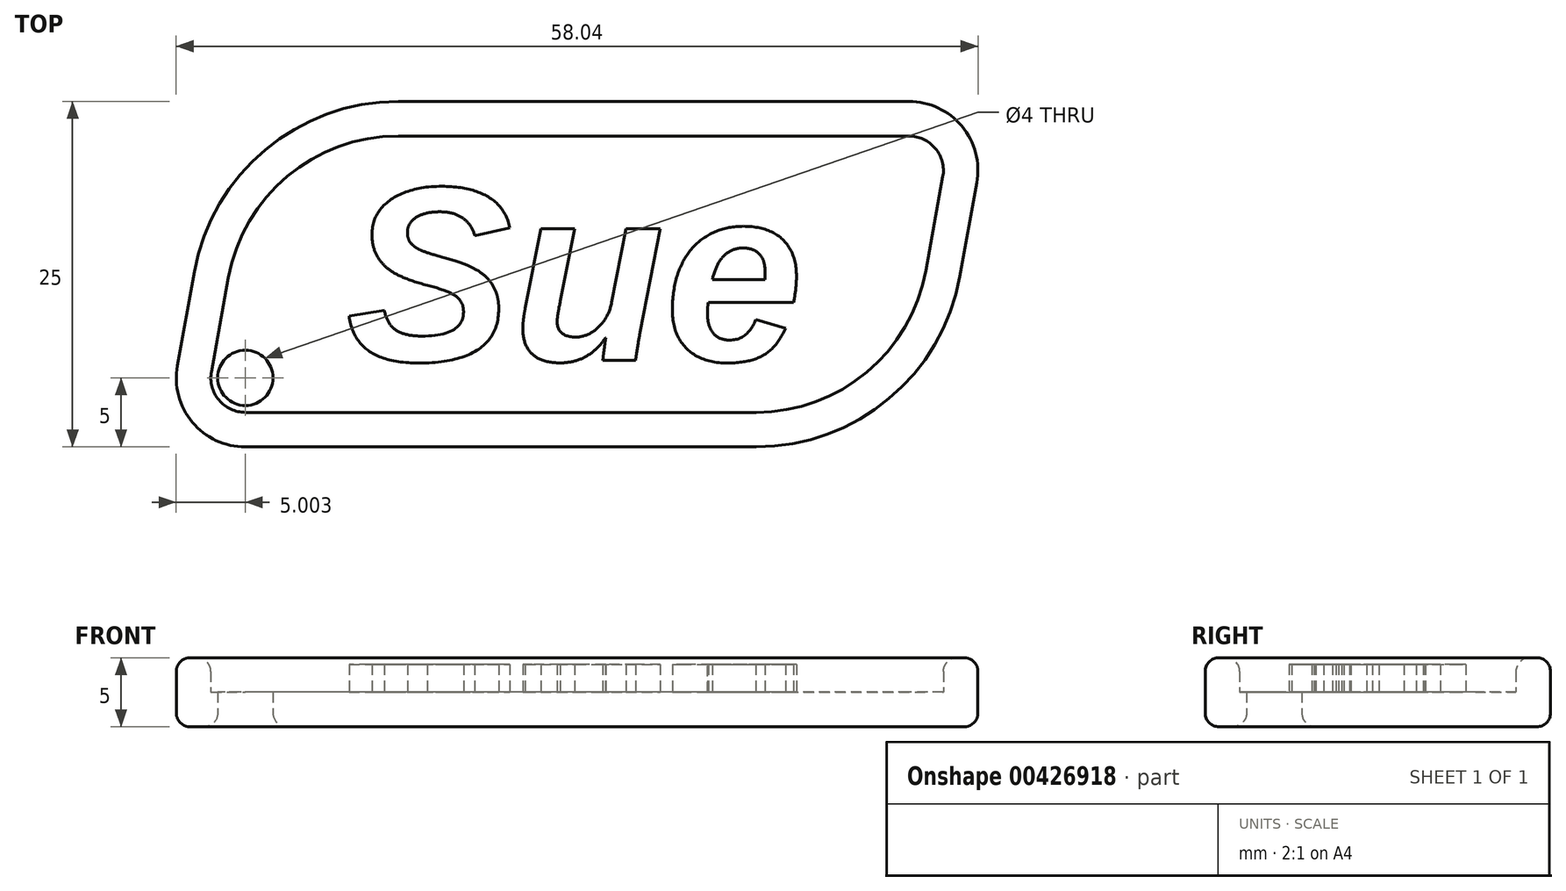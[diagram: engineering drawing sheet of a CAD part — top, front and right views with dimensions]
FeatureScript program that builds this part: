
annotation { "Feature Type Name" : "Feature", "Feature Type Description" : "" }
export const myFeature = defineFeature(function(context is Context, id is Id, definition is map)
    precondition{}
    {
        {
            var Q0;
            Q0=qCreatedBy(makeId("Top.planeOp"),FACE);
            var sketch = newSketch(context, id + "F0", { "sketchPlane" : qUnion([Q0])});
            skLineSegment(sketch, "E0.bottom", {"start": v(24.02, 12.5) * mm, "end": v(-12.95, 12.5) * mm});
            skLineSegment(sketch, "E0.top", {"start": v(12.95, -12.5) * mm, "end": v(-24.02, -12.5) * mm});
            skPoint(sketch, "E0.middle", {"position": v(0, 0) * mm});
            skLineSegment(sketch, "E1", {"start": v(-28.94, -6.61) * mm, "end": v(-27.71, 0.16) * mm});
            skLineSegment(sketch, "E2", {"start": v(28.94, 6.61) * mm, "end": v(27.71, -0.16) * mm});
            skPoint(sketch, "E3.orphan", {"position": v(-30.49, 12.5) * mm});
            skPoint(sketch, "E0.left.end.orphan", {"position": v(30.49, -12.5) * mm});
            skPoint(sketch, "E4.visualSharp", {"position": v(-25.49, 12.5) * mm});
            skArc(sketch, "E4.filletArc", {"start": v(-12.95, 12.5) * mm, "mid": v(-22.57, 9) * mm, "end": v(-27.71, 0.16) * mm});
            skPoint(sketch, "E5.visualSharp", {"position": v(25.49, -12.5) * mm});
            skArc(sketch, "E5.filletArc", {"start": v(12.95, -12.5) * mm, "mid": v(22.57, -9) * mm, "end": v(27.71, -0.16) * mm});
            skPoint(sketch, "E6.visualSharp", {"position": v(-30, -12.5) * mm});
            skArc(sketch, "E6.filletArc", {"start": v(-28.94, -6.61) * mm, "mid": v(-27.85, -10.7) * mm, "end": v(-24.02, -12.5) * mm});
            skPoint(sketch, "E7.visualSharp", {"position": v(30, 12.5) * mm});
            skArc(sketch, "E7.filletArc", {"start": v(28.94, 6.61) * mm, "mid": v(27.85, 10.7) * mm, "end": v(24.02, 12.5) * mm});
            skArc(sketch, "E8.0", {"start": v(26.48, 7.06) * mm, "mid": v(25.94, 9.1) * mm, "end": v(24.02, 10) * mm});
            skLineSegment(sketch, "E8.1", {"start": v(26.48, 7.06) * mm, "end": v(25.25, 0.28) * mm});
            skLineSegment(sketch, "E8.2", {"start": v(24.02, 10) * mm, "end": v(-12.95, 10) * mm});
            skArc(sketch, "E8.3", {"start": v(12.95, -10) * mm, "mid": v(20.97, -7.1) * mm, "end": v(25.25, 0.28) * mm});
            skArc(sketch, "E8.4", {"start": v(-12.95, 10) * mm, "mid": v(-20.97, 7.1) * mm, "end": v(-25.25, -0.28) * mm});
            skLineSegment(sketch, "E8.5", {"start": v(-26.48, -7.06) * mm, "end": v(-25.25, -0.28) * mm});
            skArc(sketch, "E8.6", {"start": v(-26.48, -7.06) * mm, "mid": v(-25.94, -9.1) * mm, "end": v(-24.02, -10) * mm});
            skLineSegment(sketch, "E8.7", {"start": v(12.95, -10) * mm, "end": v(-24.02, -10) * mm});
            skCircle(sketch, "E9", {"center": v(-24.02, -7.5) * mm, "radius": 2 * mm});
            skSolve(sketch);
        }
        {
            var Q0;
            Q0=makeQuery(id+"F0.imprint","IMPRINT",FACE,{"disambiguationData":[TD([[makeQuery(id+"F0.imprint","IMPRINT",EDGE,{"derivedFrom":sQuery(id+"F0.wireOp",EDGE,"E0.bottom")}),1.0]])]});
            extrude(context, id + "F1", {"entities" : qUnion([Q0]), "depth" : 5 * mm});
        }
        {
            var Q0;
            Q0=makeQuery(id+"F0.imprint","IMPRINT",FACE,{"disambiguationData":[TD([[makeQuery(id+"F0.imprint","IMPRINT",EDGE,{"derivedFrom":sQuery(id+"F0.wireOp",EDGE,"E8.0")}),1.0]])]});
            extrude(context, id + "F2", {"entities" : qUnion([Q0]), "operationType" : NewBodyOperationType.ADD, "depth" : 2.5 * mm});
        }
        {
            var Q0;
            Q0=makeQuery(id+"F2.opExtrude","CAP_FACE",FACE,{"disambiguationData":[OSD([sQuery(id+"F0.wireOp",EDGE,"E8.0"),sQuery(id+"F0.wireOp",EDGE,"E8.1"),sQuery(id+"F0.wireOp",EDGE,"E8.2"),sQuery(id+"F0.wireOp",EDGE,"E8.3"),sQuery(id+"F0.wireOp",EDGE,"E8.4"),sQuery(id+"F0.wireOp",EDGE,"E8.5"),sQuery(id+"F0.wireOp",EDGE,"E8.6"),sQuery(id+"F0.wireOp",EDGE,"E8.7"),sQuery(id+"F0.wireOp",EDGE,"E9")])],"isStart":false});
            var sketch = newSketch(context, id + "F3", { "sketchPlane" : qUnion([Q0])});
            skText(sketch, "E10", { "text": "Sue", "fontName": "Arimo-BoldItalic.ttf"});
            const initialGuessF3  = {"E10": [-0.01673, -0.00625, 1, 0, 0.013]};
            skSetInitialGuess(sketch, initialGuessF3);
            skSolve(sketch);
        }
        {
            var Q0;
            Q0 = qSketchRegion(id + "F3", true);
            extrude(context, id + "F4", {"entities" : qUnion([Q0]), "operationType" : NewBodyOperationType.ADD, "depth" : 2 * mm});
        }
        {
            var Q0;
            Q0=makeQuery(id+"F1.opExtrude","CAP_FACE",FACE,{"disambiguationData":[OSD([sQuery(id+"F0.wireOp",EDGE,"E0.bottom"),sQuery(id+"F0.wireOp",EDGE,"E0.top"),sQuery(id+"F0.wireOp",EDGE,"E1"),sQuery(id+"F0.wireOp",EDGE,"E2"),sQuery(id+"F0.wireOp",EDGE,"E4.filletArc"),sQuery(id+"F0.wireOp",EDGE,"E5.filletArc"),sQuery(id+"F0.wireOp",EDGE,"E6.filletArc"),sQuery(id+"F0.wireOp",EDGE,"E7.filletArc"),sQuery(id+"F0.wireOp",EDGE,"E8.0"),sQuery(id+"F0.wireOp",EDGE,"E8.1"),sQuery(id+"F0.wireOp",EDGE,"E8.2"),sQuery(id+"F0.wireOp",EDGE,"E8.3"),sQuery(id+"F0.wireOp",EDGE,"E8.4"),sQuery(id+"F0.wireOp",EDGE,"E8.5"),sQuery(id+"F0.wireOp",EDGE,"E8.6"),sQuery(id+"F0.wireOp",EDGE,"E8.7")])],"isStart":false});
            var Q1;
            {var subQ0=sQuery(id+"F0.wireOp",EDGE,"E8.7");var subQ1=sQuery(id+"F0.wireOp",EDGE,"E8.6");var subQ2=sQuery(id+"F0.wireOp",EDGE,"E8.5");var subQ3=sQuery(id+"F0.wireOp",EDGE,"E8.4");var subQ4=sQuery(id+"F0.wireOp",EDGE,"E8.3");var subQ5=sQuery(id+"F0.wireOp",EDGE,"E8.2");var subQ6=sQuery(id+"F0.wireOp",EDGE,"E8.1");var subQ7=sQuery(id+"F0.wireOp",EDGE,"E8.0");Q1=makeQuery(id+"F2.boolean.opBoolean","MERGE",FACE,{"derivedFrom":[makeQuery(id+"F1.opExtrude","CAP_FACE",FACE,{"disambiguationData":[OSD([sQuery(id+"F0.wireOp",EDGE,"E0.bottom"),sQuery(id+"F0.wireOp",EDGE,"E0.top"),sQuery(id+"F0.wireOp",EDGE,"E1"),sQuery(id+"F0.wireOp",EDGE,"E2"),sQuery(id+"F0.wireOp",EDGE,"E4.filletArc"),sQuery(id+"F0.wireOp",EDGE,"E5.filletArc"),sQuery(id+"F0.wireOp",EDGE,"E6.filletArc"),sQuery(id+"F0.wireOp",EDGE,"E7.filletArc"),subQ7,subQ6,subQ5,subQ4,subQ3,subQ2,subQ1,subQ0])],"isStart":true}),makeQuery(id+"F2.opExtrude","CAP_FACE",FACE,{"disambiguationData":[OSD([subQ7,subQ6,subQ5,subQ4,subQ3,subQ2,subQ1,subQ0,sQuery(id+"F0.wireOp",EDGE,"E9")])],"isStart":true})]});}
            fillet(context, id + "F5", {"entities" : qUnion([Q0, Q1]), "radius" : 1 * mm, "tangentPropagation" : true, "allowEdgeOverflow" : false});
        }
    });
